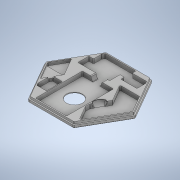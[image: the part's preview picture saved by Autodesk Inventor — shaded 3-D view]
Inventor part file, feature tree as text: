
AUTODESK INVENTOR PART (.ipt)
format: ipt  version: 2021 (Build 250183000, 183)  size: 636,928 bytes
history: native  units: mm
features: extrude x8, sketch x4, projected_geometry x4, fillet x2, other x2, plane x1, loft x1, chamfer x1
ambient origin geometry x8: Origin, YZ Plane, XZ Plane, XY Plane, X Axis, Y Axis, Z Axis, Center Point
bodies: Solid1 (feature_tree)
feature tree (23):
  extrude  "Extrusion1"  Depth=0.2mm
  extrude  "Extrusion2"  Depth=6.0mm TaperAngle=0.0deg
  extrude  "Extrusion3"  Depth=108.4mm
  extrude  "Extrusion4"  Depth=2.0mm
  extrude  "Extrusion10"  Depth=22.3mm
  extrude  "Extrusion11"  Depth=2.0mm
  extrude  "Extrusion12"  Depth=2.0mm
  extrude  "Extrusion13"  Depth=1.5mm
  plane  "Work Plane2"
  loft  "Loft2"
  fillet  "Fillet2"  Radius=3.0mm
  fillet  "Fillet3"  [1 undecoded]
  chamfer  "Chamfer1"  Distance=2.0mm
  sketch  "Sketch10"  dims[d0=102.0mm d2=0.2mm]
  projected_geometry  "Projected Loop10"
  sketch  "Sketch11"  dims[d8=1.0mm d9=0.0mm d10=6.0mm d11=0.0mm]
  projected_geometry  "Projected Loop11"
  sketch  "Sketch12"  dims[d16=108.4mm d17=42.0mm]
  projected_geometry  "Projected Loop12"
  sketch  "Sketch13"  dims[d18=64.0mm d19=43.0mm d21=22.3mm d22=19.6mm d26=65.0mm d27=1.5mm d28=1.5mm d30=3.0mm d31=0.0mm d32=2.0mm d33=0.0mm d43=0.5mm d50=35.5mm d74=0.5mm d78=0.5mm d79=0.5mm d80=0.5mm d93=0.5mm d95=0.5mm d110=1.0mm d112=1.0mm d117=22.0mm d149=0.5mm d150=0.5mm d151=0.5mm d152=3.0mm d153=0.524802mm d154=0.5mm d155=21.2mm d156=14.2mm d157=3.0mm d158=45.0deg d159=0.5mm d160=0.5mm d162=0.5mm d163=0.5mm d164=23.2mm d165=20.15mm d166=0.5mm d167=19.6mm d168=22.3mm d169=1.5mm d170=0.5mm d171=0.5mm d172=0.5mm d173=0.5mm d174=0.5mm d175=0.5mm d176=0.5mm d177=0.5mm d178=0.5mm d179=0.5mm d180=0.5mm d181=5.0mm d182=0.5mm d183=0.5mm d184=0.5mm d185=4.0mm d186=0.0mm d187=0.5mm d188=10.0mm d189=4.0mm d190=0.0mm d191=0.5mm d192=10.0mm d193=0.5mm d194=0.0mm d195=0.5mm d196=0.5mm d197=2.5mm d198=0.5mm d199=0.0mm d200=4.0mm d201=0.0mm d202=90.0deg d203=0.0mm d204=90.0deg d205=0.0mm d206=90.0deg d207=1.5mm d208=0.5mm d209=0.5mm d210=0.25mm d211=1.5mm d212=2.0mm d213=1.0mm d214=2.0mm d215=45.0deg]
  projected_geometry  "Projected Loop13"
  other  "Edges3"
  other  "Edges4"
note: 1 required parameter value undecoded (feature->parameter linkage not recoverable at this tier; creation-order binding heuristic only, values carry confidence <= 0.55)
